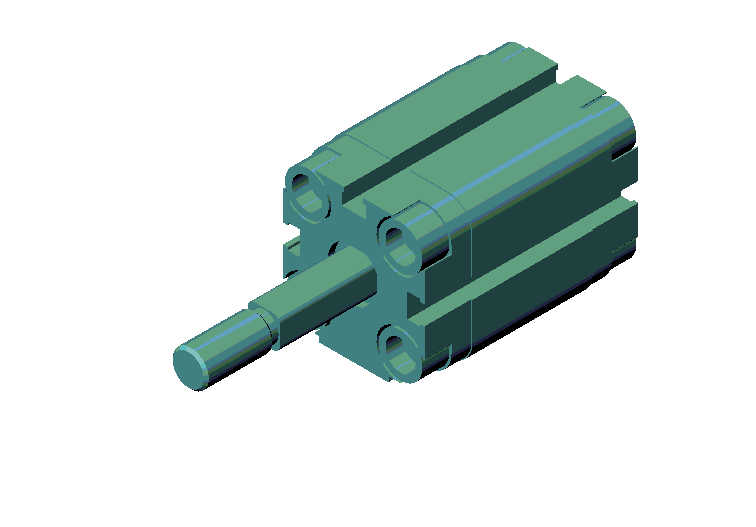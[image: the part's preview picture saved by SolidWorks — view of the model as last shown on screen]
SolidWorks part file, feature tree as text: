
SOLIDWORKS PART (.sldprt)
format: sldprt  version: not decoded by parser v0  size: 285,184 bytes
history: native  units: mm
features: sketch x16, cut_extrude x10, thread x7, extrude x6, plane x3, fillet x2, chamfer x1 (+5 scaffold rows collapsed)
feature tree (50):
  scaffold x5  (default folders/planes/origin — collapsed)
  plane  "Ebene1"
  plane  "Ebene2"
  plane  "Ebene3"
  sketch  "Skizze1"  dims[D5=7.0mm D1=20.0mm D2=40.0mm D3=20.0mm D4=40.0mm D6=41.5mm D7=20.0mm D8=10.0mm]
  extrude  "Basis-Linear austragen"  Depth=33.5mm
  sketch  "Skizze2"  dims[D1=0.3mm]
  extrude  "Aufsatz-Linear austragen1"  Depth=13mm
  sketch  "Skizze3"  dims[D1=0.3mm]
  extrude  "Aufsatz-Linear austragen2"  Depth=13mm
  sketch  "Skizze4"  dims[c1.D1=2.65mm c1.D2=3.35mm c1.D3=3.4mm c1.D4=5.05mm c1.D5=~4.590246mm c2.D5=90.0deg c3.D5=3.35mm c3.D6=2.65mm c3.D7=3.4mm c3.D8=5.05mm]
  cut_extrude  "Schnitt-Linear austragen1"  [1 undecoded]
  sketch  "Skizze5"  dims[D1=14.5mm]
  cut_extrude  "Schnitt-Linear austragen2"  Depth=2mm
  sketch  "Skizze6"  dims[D1=12.2mm D2=12.2mm D3=12.2mm D4=12.2mm D5=13.0mm]
  cut_extrude  "Schnitt-Linear austragen3"  Depth=7.5mm
  sketch  "Skizze7"  dims[D1=19.7mm]
  cut_extrude  "Schnitt-Linear austragen4"  Depth=4mm
  sketch  "Skizze8"
  cut_extrude  "Schnitt-Linear austragen5"  Depth=7.5mm
  sketch  "Skizze9"  dims[D1=8.4mm]
  cut_extrude  "Schnitt-Linear austragen6"  Depth=4.5mm
  sketch  "Skizze10"  dims[D1=4.13mm]
  cut_extrude  "Schnitt-Linear austragen7"  [1 undecoded]
  thread  "Gewindedarstellung1"  [2 undecoded]
  cut_extrude  "Schnitt-Linear austragen8"  [1 undecoded]
  sketch  "Skizze11"  dims[c1.D1=4.5mm c2.D1=59.5mm c2.D2=5.0mm]
  thread  "Gewindedarstellung2"  Diameter=59.5mm  [1 undecoded]
  thread  "Gewindedarstellung3"  Diameter=59.5mm  [1 undecoded]
  thread  "Gewindedarstellung4"  Diameter=59.5mm  [1 undecoded]
  sketch  "Skizze12"  dims[c1.D1=~3.116508mm c1.D2=~3.116508mm c1.D3=4.13mm c1.D4=4.13mm c2.D1=43.0mm c2.D2=21.5mm]
  cut_extrude  "Schnitt-Linear austragen9"  [1 undecoded]
  thread  "Gewindedarstellung5"  Diameter=9mm  [1 undecoded]
  thread  "Gewindedarstellung6"  Diameter=9mm  [1 undecoded]
  sketch  "Skizze13"  dims[D1=1.5mm D2=1.5mm]
  cut_extrude  "Schnitt-Linear austragen10"  Depth=3mm
  sketch  "Skizze14"  dims[D5=2.0mm D1=9.0mm D2=9.0mm D3=4.5mm D4=4.5mm]
  extrude  "Aufsatz-Linear austragen3"  Depth=27mm
  sketch  "Skizze15"  dims[D1=~18.384776mm]
  extrude  "Aufsatz-Linear austragen4"  Depth=2mm
  sketch  "Skizze16"  dims[D1=10.0mm]
  extrude  "Aufsatz-Linear austragen5"  [1 undecoded]
  thread  "Gewindedarstellung7"  [2 undecoded]
  chamfer  "Fase1"  Distance=0.7mm Angle=45deg
  fillet  "Verrundung6"  Radius=0.2mm
  fillet  "Verrundung7"  Radius=0.2mm
decode coverage: 34 of 42 modeling features carry decoded parameters
note: ~ marks probable driven/reference dimensions
note: 14 parameter values undecoded
summary: no parameter record found for 7 features
note: suppression state not decoded; provenance and decode notes live in map.json
